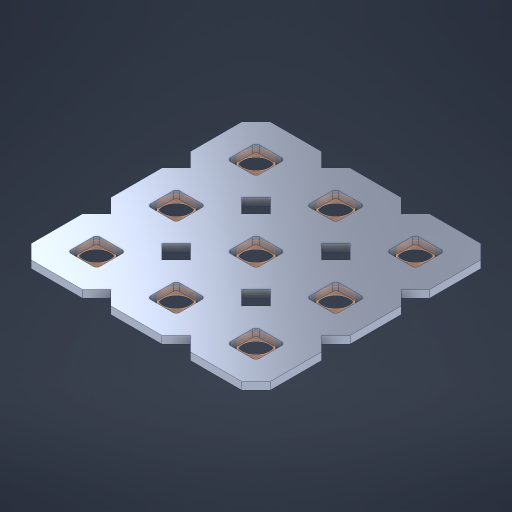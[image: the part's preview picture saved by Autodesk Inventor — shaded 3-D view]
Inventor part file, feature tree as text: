
AUTODESK INVENTOR PART (.ipt)
format: ipt  version: 2023 (Build 270158000, 158)  size: 354,304 bytes
history: native  units: in
note: dims shown in document units (in); Inventor stores cm internally (conversion verified against a paired STEP export)
features: other x10, extrude x8, sketch x2, pattern_linear x1
ambient origin geometry x8: Origin, YZ Plane, XZ Plane, XY Plane, X Axis, Y Axis, Z Axis, Center Point
bodies: Solid1 (feature_tree), Body (feature_tree)
feature tree (21):
  pattern_linear  "Rectangular Pattern1"  Spacing1=0.09in  [1 undecoded]
  sketch  "Sketch1"  dims[d1=0.5in]
  sketch  "Sketch2"  dims[d2=0.182in d3=0.09in d4=0.09in d5=0.09in d6=0.09in d7=0.09in d8=0.09in d9=0.09in d10=0.09in d11=0.02in d13=0.0in d14=0.172in d15=0.0625in d16=0.0in d19=0.5in d22=0.5in]
  other  "Srf1"
  other  "Srf126"
  other  "Srf127"
  other  "Srf268"
  other  "Srf269"
  other  "Srf270"
  other  "Srf293"
  other  "Srf294"
  other  "Srf295"
  other  "Circle"
  extrude  "ExtrusionSrf126"  Depth=0.09in
  extrude  "ExtrusionSrf127"  Depth=0.09in
  extrude  "ExtrusionSrf268"  Depth=0.09in
  extrude  "ExtrusionSrf269"  Depth=0.09in
  extrude  "ExtrusionSrf270"  Depth=0.09in
  extrude  "ExtrusionSrf293"  Depth=0.09in
  extrude  "ExtrusionSrf294"  Depth=0.09in
  extrude  "ExtrusionSrf295"  Depth=0.02in
note: 1 required parameter value undecoded (feature->parameter linkage not recoverable at this tier; creation-order binding heuristic only, values carry confidence <= 0.55)
